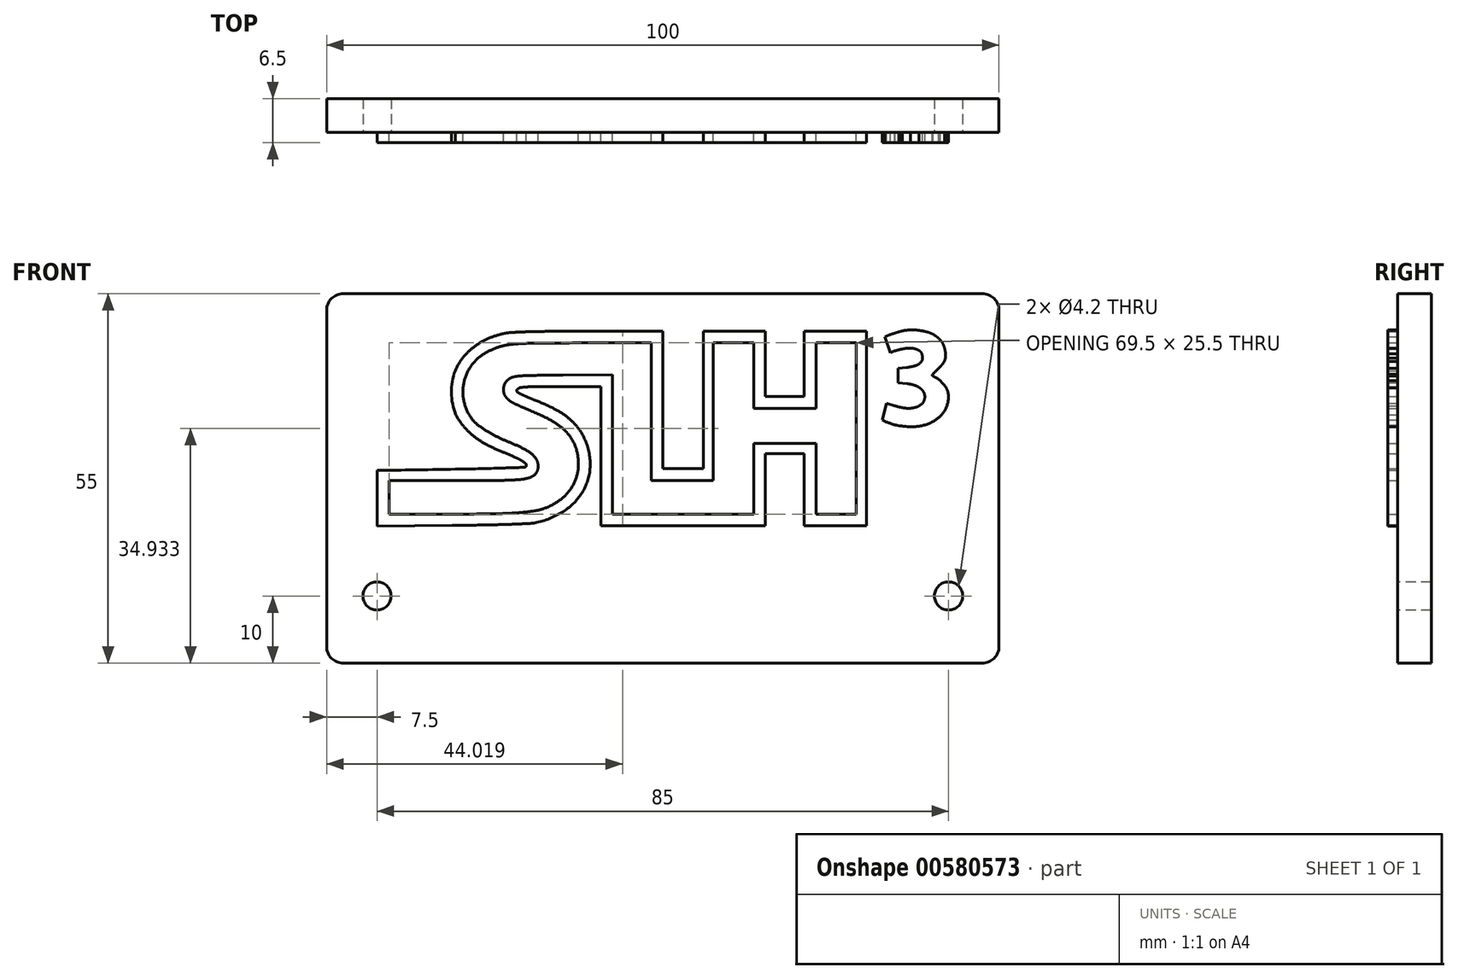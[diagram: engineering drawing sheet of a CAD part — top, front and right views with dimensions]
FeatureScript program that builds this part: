
annotation { "Feature Type Name" : "Feature", "Feature Type Description" : "" }
export const myFeature = defineFeature(function(context is Context, id is Id, definition is map)
    precondition{}
    {
        {
            var Q0;
            Q0=qCreatedBy(makeId("Front.planeOp"),FACE);
            var sketch = newSketch(context, id + "F0", { "sketchPlane" : qUnion([Q0])});
            skArc(sketch, "E0", {"start": v(147.3, 58.44) * mm, "mid": v(144.9, 58.22) * mm, "end": v(142.5, 57.82) * mm});
            skArc(sketch, "E1", {"start": v(142.5, 57.82) * mm, "mid": v(141.63, 57.59) * mm, "end": v(140.75, 57.35) * mm});
            skArc(sketch, "E2", {"start": v(140.75, 57.35) * mm, "mid": v(139.8, 57.05) * mm, "end": v(138.84, 56.75) * mm});
            skArc(sketch, "E3", {"start": v(138.84, 56.75) * mm, "mid": v(137.83, 56.42) * mm, "end": v(136.83, 56.09) * mm});
            skArc(sketch, "E4", {"start": v(136.83, 56.09) * mm, "mid": v(134.45, 55.26) * mm, "end": v(132.1, 54.33) * mm});
            skArc(sketch, "E5", {"start": v(135.3, 44.79) * mm, "mid": v(138.92, 46.14) * mm, "end": v(142.68, 47.08) * mm});
            skArc(sketch, "E6", {"start": v(142.68, 47.08) * mm, "mid": v(145.3, 47.46) * mm, "end": v(147.96, 47.48) * mm});
            skArc(sketch, "E7", {"start": v(147.96, 47.48) * mm, "mid": v(150, 47.16) * mm, "end": v(151.95, 46.48) * mm});
            skArc(sketch, "E8", {"start": v(151.95, 46.48) * mm, "mid": v(153.25, 45.54) * mm, "end": v(154.1, 44.19) * mm});
            skArc(sketch, "E9", {"start": v(154.1, 44.19) * mm, "mid": v(154.46, 42.68) * mm, "end": v(154.45, 41.13) * mm});
            skArc(sketch, "E10", {"start": v(154.45, 41.13) * mm, "mid": v(154.03, 39.82) * mm, "end": v(153.18, 38.74) * mm});
            skArc(sketch, "E11", {"start": v(153.18, 38.74) * mm, "mid": v(151.73, 37.71) * mm, "end": v(150.09, 37.04) * mm});
            skArc(sketch, "E12", {"start": v(150.09, 37.04) * mm, "mid": v(147.56, 36.44) * mm, "end": v(145, 36.04) * mm});
            skLineSegment(sketch, "E13", {"start": v(145, 36.04) * mm, "end": v(140.08, 35.45) * mm});
            skLineSegment(sketch, "E14", {"start": v(140.08, 35.45) * mm, "end": v(140.08, 31.23) * mm});
            skLineSegment(sketch, "E15", {"start": v(140.08, 31.23) * mm, "end": v(140.08, 27.01) * mm});
            skLineSegment(sketch, "E16", {"start": v(140.08, 27.01) * mm, "end": v(145.31, 26.4) * mm});
            skArc(sketch, "E17", {"start": v(145.31, 26.4) * mm, "mid": v(147.5, 26.03) * mm, "end": v(149.65, 25.5) * mm});
            skArc(sketch, "E18", {"start": v(149.65, 25.5) * mm, "mid": v(151.33, 24.84) * mm, "end": v(152.88, 23.93) * mm});
            skArc(sketch, "E19", {"start": v(152.88, 23.93) * mm, "mid": v(154.03, 22.94) * mm, "end": v(154.95, 21.74) * mm});
            skArc(sketch, "E20", {"start": v(154.95, 21.74) * mm, "mid": v(155.57, 20.42) * mm, "end": v(155.88, 19) * mm});
            skArc(sketch, "E21", {"start": v(155.88, 19) * mm, "mid": v(155.68, 16.9) * mm, "end": v(154.7, 15.06) * mm});
            skArc(sketch, "E22", {"start": v(154.7, 15.06) * mm, "mid": v(152.96, 13.47) * mm, "end": v(150.85, 12.44) * mm});
            skArc(sketch, "E23", {"start": v(150.85, 12.44) * mm, "mid": v(147.9, 11.8) * mm, "end": v(144.88, 11.77) * mm});
            skArc(sketch, "E24", {"start": v(144.88, 11.77) * mm, "mid": v(141.4, 12.3) * mm, "end": v(138.02, 13.25) * mm});
            skArc(sketch, "E25", {"start": v(130.58, 4.7) * mm, "mid": v(134.35, 3.08) * mm, "end": v(138.27, 1.86) * mm});
            skArc(sketch, "E26", {"start": v(138.27, 1.86) * mm, "mid": v(144.65, 0.87) * mm, "end": v(151.1, 0.91) * mm});
            skArc(sketch, "E27", {"start": v(151.1, 0.91) * mm, "mid": v(156.72, 2.08) * mm, "end": v(161.92, 4.5) * mm});
            skArc(sketch, "E28", {"start": v(161.92, 4.5) * mm, "mid": v(165.7, 7.66) * mm, "end": v(168.44, 11.76) * mm});
            skArc(sketch, "E29", {"start": v(168.44, 11.76) * mm, "mid": v(169.8, 16.35) * mm, "end": v(169.66, 21.14) * mm});
            skArc(sketch, "E30", {"start": v(169.66, 21.14) * mm, "mid": v(169.24, 22.6) * mm, "end": v(168.57, 23.97) * mm});
            skArc(sketch, "E31", {"start": v(168.57, 23.97) * mm, "mid": v(166.9, 26.2) * mm, "end": v(165.02, 28.24) * mm});
            skArc(sketch, "E32", {"start": v(165.02, 28.24) * mm, "mid": v(162.97, 29.65) * mm, "end": v(160.8, 30.87) * mm});
            skArc(sketch, "E33", {"start": v(160.8, 30.87) * mm, "mid": v(160.38, 31.45) * mm, "end": v(160.66, 32.1) * mm});
            skArc(sketch, "E34", {"start": v(160.66, 32.1) * mm, "mid": v(162.36, 33.8) * mm, "end": v(164.08, 35.5) * mm});
            skArc(sketch, "E35", {"start": v(164.08, 35.5) * mm, "mid": v(165.17, 36.63) * mm, "end": v(166.22, 37.8) * mm});
            skArc(sketch, "E36", {"start": v(166.22, 37.8) * mm, "mid": v(166.84, 38.64) * mm, "end": v(167.35, 39.53) * mm});
            skArc(sketch, "E37", {"start": v(167.35, 39.53) * mm, "mid": v(167.8, 40.5) * mm, "end": v(168.09, 41.53) * mm});
            skArc(sketch, "E38", {"start": v(168.09, 41.53) * mm, "mid": v(168.2, 42.88) * mm, "end": v(168.2, 44.24) * mm});
            skArc(sketch, "E39", {"start": v(168.2, 44.24) * mm, "mid": v(168, 45.88) * mm, "end": v(167.63, 47.49) * mm});
            skArc(sketch, "E40", {"start": v(167.63, 47.49) * mm, "mid": v(167.09, 49.15) * mm, "end": v(166.3, 50.72) * mm});
            skArc(sketch, "E41", {"start": v(166.3, 50.72) * mm, "mid": v(165.28, 52.17) * mm, "end": v(164.05, 53.45) * mm});
            skArc(sketch, "E42", {"start": v(164.05, 53.45) * mm, "mid": v(162.51, 54.68) * mm, "end": v(160.85, 55.74) * mm});
            skArc(sketch, "E43", {"start": v(160.85, 55.74) * mm, "mid": v(159.13, 56.56) * mm, "end": v(157.3, 57.16) * mm});
            skArc(sketch, "E44", {"start": v(157.3, 57.16) * mm, "mid": v(154.84, 57.72) * mm, "end": v(152.34, 58.13) * mm});
            skArc(sketch, "E45", {"start": v(152.34, 58.13) * mm, "mid": v(149.83, 58.36) * mm, "end": v(147.3, 58.44) * mm});
            skArc(sketch, "E46", {"start": v(-94.8, 56.19) * mm, "mid": v(-99.37, 54.96) * mm, "end": v(-103.8, 53.28) * mm});
            skArc(sketch, "E47", {"start": v(-103.8, 53.28) * mm, "mid": v(-107.86, 51.23) * mm, "end": v(-111.67, 48.76) * mm});
            skArc(sketch, "E48", {"start": v(-111.67, 48.76) * mm, "mid": v(-115.04, 45.97) * mm, "end": v(-118.08, 42.81) * mm});
            skArc(sketch, "E49", {"start": v(-118.08, 42.81) * mm, "mid": v(-121.12, 38.65) * mm, "end": v(-123.5, 34.08) * mm});
            skArc(sketch, "E50", {"start": v(-123.1, 7.94) * mm, "mid": v(-120.99, 4.39) * mm, "end": v(-118.53, 1.07) * mm});
            skArc(sketch, "E51", {"start": v(-118.53, 1.07) * mm, "mid": v(-115.75, -1.97) * mm, "end": v(-112.67, -4.7) * mm});
            skArc(sketch, "E52", {"start": v(-112.67, -4.7) * mm, "mid": v(-109, -7.38) * mm, "end": v(-105.1, -9.7) * mm});
            skArc(sketch, "E53", {"start": v(-105.1, -9.7) * mm, "mid": v(-100.3, -12.1) * mm, "end": v(-95.37, -14.24) * mm});
            skArc(sketch, "E54", {"start": v(-95.37, -14.24) * mm, "mid": v(-91.84, -15.69) * mm, "end": v(-88.34, -17.2) * mm});
            skArc(sketch, "E55", {"start": v(-88.34, -17.2) * mm, "mid": v(-86.15, -18.23) * mm, "end": v(-84.03, -19.4) * mm});
            skArc(sketch, "E56", {"start": v(-84.03, -19.4) * mm, "mid": v(-82.76, -20.23) * mm, "end": v(-81.57, -21.17) * mm});
            skArc(sketch, "E57", {"start": v(-81.57, -21.17) * mm, "mid": v(-81.17, -21.82) * mm, "end": v(-81.2, -22.58) * mm});
            skArc(sketch, "E58", {"start": v(-81.2, -22.58) * mm, "mid": v(-81.6, -23.16) * mm, "end": v(-82.27, -23.4) * mm});
            skArc(sketch, "E59", {"start": v(-82.27, -23.4) * mm, "mid": v(-89.42, -23.65) * mm, "end": v(-96.57, -23.9) * mm});
            skArc(sketch, "E60", {"start": v(-96.57, -23.9) * mm, "mid": v(-107.38, -24.2) * mm, "end": v(-118.18, -24.43) * mm});
            skArc(sketch, "E61", {"start": v(-118.18, -24.43) * mm, "mid": v(-139.68, -24.8) * mm, "end": v(-161.17, -25.13) * mm});
            skLineSegment(sketch, "E62", {"start": v(-161.17, -25.13) * mm, "end": v(-169.92, -25.27) * mm});
            skLineSegment(sketch, "E63", {"start": v(-169.92, -25.27) * mm, "end": v(-169.92, -41.9) * mm});
            skLineSegment(sketch, "E64", {"start": v(-169.92, -41.9) * mm, "end": v(-169.92, -58.54) * mm});
            skLineSegment(sketch, "E65", {"start": v(-169.92, -58.54) * mm, "end": v(-125.17, -58.01) * mm});
            skArc(sketch, "E66", {"start": v(-125.17, -58.01) * mm, "mid": v(-115.04, -57.88) * mm, "end": v(-104.91, -57.7) * mm});
            skArc(sketch, "E67", {"start": v(-104.91, -57.7) * mm, "mid": v(-97.51, -57.54) * mm, "end": v(-90.11, -57.31) * mm});
            skArc(sketch, "E68", {"start": v(-90.11, -57.31) * mm, "mid": v(-84.7, -57.1) * mm, "end": v(-79.27, -56.85) * mm});
            skArc(sketch, "E69", {"start": v(-79.27, -56.85) * mm, "mid": v(-77.08, -56.64) * mm, "end": v(-74.92, -56.25) * mm});
            skArc(sketch, "E70", {"start": v(-74.92, -56.25) * mm, "mid": v(-66.24, -53.43) * mm, "end": v(-58.23, -49.06) * mm});
            skArc(sketch, "E71", {"start": v(-58.23, -49.06) * mm, "mid": v(-51.9, -43.6) * mm, "end": v(-47.03, -36.8) * mm});
            skArc(sketch, "E72", {"start": v(-47.03, -36.8) * mm, "mid": v(-44.12, -29.35) * mm, "end": v(-43.18, -21.4) * mm});
            skArc(sketch, "E73", {"start": v(-43.18, -21.4) * mm, "mid": v(-44.2, -13.14) * mm, "end": v(-47.06, -5.32) * mm});
            skArc(sketch, "E74", {"start": v(-47.06, -5.32) * mm, "mid": v(-49.08, -1.82) * mm, "end": v(-51.5, 1.41) * mm});
            skArc(sketch, "E75", {"start": v(-51.5, 1.41) * mm, "mid": v(-54.35, 4.4) * mm, "end": v(-57.51, 7.02) * mm});
            skArc(sketch, "E76", {"start": v(-57.51, 7.02) * mm, "mid": v(-61.55, 9.74) * mm, "end": v(-65.82, 12.07) * mm});
            skArc(sketch, "E77", {"start": v(-65.82, 12.07) * mm, "mid": v(-71.57, 14.73) * mm, "end": v(-77.42, 17.15) * mm});
            skArc(sketch, "E78", {"start": v(-77.42, 17.15) * mm, "mid": v(-78.84, 17.71) * mm, "end": v(-80.25, 18.3) * mm});
            skArc(sketch, "E79", {"start": v(-80.25, 18.3) * mm, "mid": v(-81.6, 18.89) * mm, "end": v(-82.95, 19.5) * mm});
            skArc(sketch, "E80", {"start": v(-82.95, 19.5) * mm, "mid": v(-84.1, 20.05) * mm, "end": v(-85.23, 20.6) * mm});
            skArc(sketch, "E81", {"start": v(-85.23, 20.6) * mm, "mid": v(-85.84, 20.95) * mm, "end": v(-86.42, 21.34) * mm});
            skArc(sketch, "E82", {"start": v(-86.42, 21.34) * mm, "mid": v(-86.85, 22.1) * mm, "end": v(-86.6, 22.92) * mm});
            skArc(sketch, "E83", {"start": v(-86.6, 22.92) * mm, "mid": v(-85.66, 23.7) * mm, "end": v(-84.5, 24.07) * mm});
            skArc(sketch, "E84", {"start": v(-84.5, 24.07) * mm, "mid": v(-80.93, 24.44) * mm, "end": v(-77.35, 24.6) * mm});
            skArc(sketch, "E85", {"start": v(-77.35, 24.6) * mm, "mid": v(-69.26, 24.68) * mm, "end": v(-61.17, 24.72) * mm});
            skLineSegment(sketch, "E86", {"start": v(-61.17, 24.72) * mm, "end": v(-36.92, 24.73) * mm});
            skLineSegment(sketch, "E87", {"start": v(-36.92, 24.73) * mm, "end": v(-36.92, -16.77) * mm});
            skLineSegment(sketch, "E88", {"start": v(-36.92, -16.77) * mm, "end": v(-36.92, -58.27) * mm});
            skLineSegment(sketch, "E89", {"start": v(-36.92, -58.27) * mm, "end": v(12.08, -58.27) * mm});
            skLineSegment(sketch, "E90", {"start": v(12.08, -58.27) * mm, "end": v(61.08, -58.27) * mm});
            skLineSegment(sketch, "E91", {"start": v(61.08, -58.27) * mm, "end": v(61.08, -36.77) * mm});
            skLineSegment(sketch, "E92", {"start": v(61.08, -36.77) * mm, "end": v(61.08, -15.27) * mm});
            skLineSegment(sketch, "E93", {"start": v(61.08, -15.27) * mm, "end": v(72.58, -15.27) * mm});
            skLineSegment(sketch, "E94", {"start": v(72.58, -15.27) * mm, "end": v(84.08, -15.27) * mm});
            skLineSegment(sketch, "E95", {"start": v(84.08, -15.27) * mm, "end": v(84.08, -36.77) * mm});
            skLineSegment(sketch, "E96", {"start": v(84.08, -36.77) * mm, "end": v(84.08, -58.27) * mm});
            skLineSegment(sketch, "E97", {"start": v(84.08, -58.27) * mm, "end": v(102.58, -58.27) * mm});
            skLineSegment(sketch, "E98", {"start": v(102.58, -58.27) * mm, "end": v(121.08, -58.27) * mm});
            skLineSegment(sketch, "E99", {"start": v(121.08, -58.27) * mm, "end": v(121.08, -0.27) * mm});
            skLineSegment(sketch, "E100", {"start": v(121.08, -0.27) * mm, "end": v(121.08, 57.73) * mm});
            skLineSegment(sketch, "E101", {"start": v(121.08, 57.73) * mm, "end": v(102.58, 57.73) * mm});
            skLineSegment(sketch, "E102", {"start": v(102.58, 57.73) * mm, "end": v(84.08, 57.73) * mm});
            skLineSegment(sketch, "E103", {"start": v(84.08, 57.73) * mm, "end": v(84.08, 38.23) * mm});
            skLineSegment(sketch, "E104", {"start": v(84.08, 38.23) * mm, "end": v(84.08, 18.73) * mm});
            skLineSegment(sketch, "E105", {"start": v(84.08, 18.73) * mm, "end": v(72.58, 18.73) * mm});
            skLineSegment(sketch, "E106", {"start": v(72.58, 18.73) * mm, "end": v(61.08, 18.73) * mm});
            skLineSegment(sketch, "E107", {"start": v(61.08, 18.73) * mm, "end": v(61.08, 38.23) * mm});
            skLineSegment(sketch, "E108", {"start": v(61.08, 38.23) * mm, "end": v(61.08, 57.73) * mm});
            skLineSegment(sketch, "E109", {"start": v(61.08, 57.73) * mm, "end": v(42.58, 57.73) * mm});
            skLineSegment(sketch, "E110", {"start": v(42.58, 57.73) * mm, "end": v(24.08, 57.73) * mm});
            skLineSegment(sketch, "E111", {"start": v(24.08, 57.73) * mm, "end": v(24.08, 16.73) * mm});
            skLineSegment(sketch, "E112", {"start": v(24.08, 16.73) * mm, "end": v(24.08, -24.27) * mm});
            skLineSegment(sketch, "E113", {"start": v(24.08, -24.27) * mm, "end": v(12.08, -24.27) * mm});
            skLineSegment(sketch, "E114", {"start": v(12.08, -24.27) * mm, "end": v(0.08, -24.27) * mm});
            skLineSegment(sketch, "E115", {"start": v(0.08, -24.27) * mm, "end": v(0.08, 16.73) * mm});
            skLineSegment(sketch, "E116", {"start": v(0.08, 16.73) * mm, "end": v(0.08, 57.73) * mm});
            skLineSegment(sketch, "E117", {"start": v(0.08, 57.73) * mm, "end": v(-44.17, 57.65) * mm});
            skArc(sketch, "E118", {"start": v(-44.17, 57.65) * mm, "mid": v(-55.24, 57.62) * mm, "end": v(-66.31, 57.55) * mm});
            skArc(sketch, "E119", {"start": v(-66.31, 57.55) * mm, "mid": v(-73.3, 57.46) * mm, "end": v(-80.3, 57.3) * mm});
            skArc(sketch, "E120", {"start": v(-80.3, 57.3) * mm, "mid": v(-85.01, 57.12) * mm, "end": v(-89.72, 56.88) * mm});
            skArc(sketch, "E121", {"start": v(-89.72, 56.88) * mm, "mid": v(-92.27, 56.63) * mm, "end": v(-94.8, 56.19) * mm});
            skLineSegment(sketch, "E122", {"start": v(-6.92, 9.73) * mm, "end": v(-6.92, -31.27) * mm});
            skLineSegment(sketch, "E123", {"start": v(-6.92, -31.27) * mm, "end": v(11.58, -31.27) * mm});
            skLineSegment(sketch, "E124", {"start": v(11.58, -31.27) * mm, "end": v(30.08, -31.27) * mm});
            skLineSegment(sketch, "E125", {"start": v(30.08, -31.27) * mm, "end": v(30.08, 9.73) * mm});
            skLineSegment(sketch, "E126", {"start": v(30.08, 9.73) * mm, "end": v(30.08, 50.73) * mm});
            skLineSegment(sketch, "E127", {"start": v(30.08, 50.73) * mm, "end": v(42.08, 50.73) * mm});
            skLineSegment(sketch, "E128", {"start": v(42.08, 50.73) * mm, "end": v(54.08, 50.73) * mm});
            skLineSegment(sketch, "E129", {"start": v(54.08, 50.73) * mm, "end": v(54.08, 31.23) * mm});
            skLineSegment(sketch, "E130", {"start": v(54.08, 31.23) * mm, "end": v(54.08, 11.73) * mm});
            skLineSegment(sketch, "E131", {"start": v(54.08, 11.73) * mm, "end": v(72.58, 11.73) * mm});
            skLineSegment(sketch, "E132", {"start": v(72.58, 11.73) * mm, "end": v(91.08, 11.73) * mm});
            skLineSegment(sketch, "E133", {"start": v(91.08, 11.73) * mm, "end": v(91.08, 31.23) * mm});
            skLineSegment(sketch, "E134", {"start": v(91.08, 31.23) * mm, "end": v(91.08, 50.73) * mm});
            skLineSegment(sketch, "E135", {"start": v(91.08, 50.73) * mm, "end": v(103.08, 50.73) * mm});
            skLineSegment(sketch, "E136", {"start": v(103.08, 50.73) * mm, "end": v(115.08, 50.73) * mm});
            skLineSegment(sketch, "E137", {"start": v(115.08, 50.73) * mm, "end": v(115.08, -0.27) * mm});
            skLineSegment(sketch, "E138", {"start": v(115.08, -0.27) * mm, "end": v(115.08, -51.27) * mm});
            skLineSegment(sketch, "E139", {"start": v(115.08, -51.27) * mm, "end": v(103.08, -51.27) * mm});
            skLineSegment(sketch, "E140", {"start": v(103.08, -51.27) * mm, "end": v(91.08, -51.27) * mm});
            skLineSegment(sketch, "E141", {"start": v(91.08, -51.27) * mm, "end": v(91.08, -30.27) * mm});
            skLineSegment(sketch, "E142", {"start": v(91.08, -30.27) * mm, "end": v(91.08, -9.27) * mm});
            skLineSegment(sketch, "E143", {"start": v(91.08, -9.27) * mm, "end": v(72.58, -9.27) * mm});
            skLineSegment(sketch, "E144", {"start": v(72.58, -9.27) * mm, "end": v(54.08, -9.27) * mm});
            skLineSegment(sketch, "E145", {"start": v(54.08, -9.27) * mm, "end": v(54.08, -30.27) * mm});
            skLineSegment(sketch, "E146", {"start": v(54.08, -30.27) * mm, "end": v(54.08, -51.27) * mm});
            skLineSegment(sketch, "E147", {"start": v(54.08, -51.27) * mm, "end": v(12.08, -51.27) * mm});
            skLineSegment(sketch, "E148", {"start": v(12.08, -51.27) * mm, "end": v(-29.92, -51.27) * mm});
            skLineSegment(sketch, "E149", {"start": v(-29.92, -51.27) * mm, "end": v(-29.92, -9.71) * mm});
            skLineSegment(sketch, "E150", {"start": v(-29.92, -9.71) * mm, "end": v(-29.92, 31.84) * mm});
            skLineSegment(sketch, "E151", {"start": v(-29.92, 31.84) * mm, "end": v(-59.35, 31.54) * mm});
            skArc(sketch, "E152", {"start": v(-59.35, 31.54) * mm, "mid": v(-68.59, 31.43) * mm, "end": v(-77.82, 31.3) * mm});
            skArc(sketch, "E153", {"start": v(-77.82, 31.3) * mm, "mid": v(-81.4, 31.2) * mm, "end": v(-85, 30.98) * mm});
            skArc(sketch, "E154", {"start": v(-85, 30.98) * mm, "mid": v(-87, 30.75) * mm, "end": v(-88.97, 30.36) * mm});
            skArc(sketch, "E155", {"start": v(-88.97, 30.36) * mm, "mid": v(-90.35, 29.88) * mm, "end": v(-91.6, 29.13) * mm});
            skArc(sketch, "E156", {"start": v(-91.6, 29.13) * mm, "mid": v(-92.29, 28.57) * mm, "end": v(-92.92, 27.95) * mm});
            skArc(sketch, "E157", {"start": v(-92.92, 27.95) * mm, "mid": v(-93.42, 27.34) * mm, "end": v(-93.84, 26.68) * mm});
            skArc(sketch, "E158", {"start": v(-93.84, 26.68) * mm, "mid": v(-94.18, 25.95) * mm, "end": v(-94.43, 25.2) * mm});
            skArc(sketch, "E159", {"start": v(-94.43, 25.2) * mm, "mid": v(-94.62, 24.3) * mm, "end": v(-94.73, 23.39) * mm});
            skArc(sketch, "E160", {"start": v(-94.73, 23.39) * mm, "mid": v(-94.69, 21.74) * mm, "end": v(-94.29, 20.15) * mm});
            skArc(sketch, "E161", {"start": v(-94.29, 20.15) * mm, "mid": v(-93.54, 18.68) * mm, "end": v(-92.5, 17.41) * mm});
            skArc(sketch, "E162", {"start": v(-92.5, 17.41) * mm, "mid": v(-90.83, 16.03) * mm, "end": v(-88.98, 14.9) * mm});
            skArc(sketch, "E163", {"start": v(-88.98, 14.9) * mm, "mid": v(-86.09, 13.48) * mm, "end": v(-83.13, 12.2) * mm});
            skArc(sketch, "E164", {"start": v(-83.13, 12.2) * mm, "mid": v(-76.1, 9.22) * mm, "end": v(-69.2, 5.99) * mm});
            skArc(sketch, "E165", {"start": v(-69.2, 5.99) * mm, "mid": v(-64.63, 3.45) * mm, "end": v(-60.37, 0.44) * mm});
            skArc(sketch, "E166", {"start": v(-60.37, 0.44) * mm, "mid": v(-57.36, -2.33) * mm, "end": v(-54.8, -5.53) * mm});
            skArc(sketch, "E167", {"start": v(-54.8, -5.53) * mm, "mid": v(-52.8, -9.04) * mm, "end": v(-51.36, -12.83) * mm});
            skArc(sketch, "E168", {"start": v(-51.36, -12.83) * mm, "mid": v(-50.33, -18.12) * mm, "end": v(-50.26, -23.51) * mm});
            skArc(sketch, "E169", {"start": v(-50.26, -23.51) * mm, "mid": v(-51.18, -28.63) * mm, "end": v(-53.1, -33.46) * mm});
            skArc(sketch, "E170", {"start": v(-53.1, -33.46) * mm, "mid": v(-56, -37.9) * mm, "end": v(-59.7, -41.69) * mm});
            skArc(sketch, "E171", {"start": v(-59.7, -41.69) * mm, "mid": v(-64.29, -44.96) * mm, "end": v(-69.35, -47.44) * mm});
            skArc(sketch, "E172", {"start": v(-69.35, -47.44) * mm, "mid": v(-72.87, -48.6) * mm, "end": v(-76.49, -49.38) * mm});
            skArc(sketch, "E173", {"start": v(-76.49, -49.38) * mm, "mid": v(-81.5, -50.05) * mm, "end": v(-86.52, -50.5) * mm});
            skArc(sketch, "E174", {"start": v(-86.52, -50.5) * mm, "mid": v(-93.97, -50.9) * mm, "end": v(-101.43, -51.1) * mm});
            skArc(sketch, "E175", {"start": v(-101.43, -51.1) * mm, "mid": v(-113.71, -51.23) * mm, "end": v(-126, -51.27) * mm});
            skLineSegment(sketch, "E176", {"start": v(-126, -51.27) * mm, "end": v(-162.92, -51.27) * mm});
            skLineSegment(sketch, "E177", {"start": v(-162.92, -51.27) * mm, "end": v(-162.92, -41.27) * mm});
            skLineSegment(sketch, "E178", {"start": v(-162.92, -41.27) * mm, "end": v(-162.92, -31.27) * mm});
            skLineSegment(sketch, "E179", {"start": v(-162.92, -31.27) * mm, "end": v(-122.9, -31.27) * mm});
            skArc(sketch, "E180", {"start": v(-122.9, -31.27) * mm, "mid": v(-108.61, -31.24) * mm, "end": v(-94.33, -31.15) * mm});
            skArc(sketch, "E181", {"start": v(-94.33, -31.15) * mm, "mid": v(-88.88, -30.96) * mm, "end": v(-83.45, -30.5) * mm});
            skArc(sketch, "E182", {"start": v(-83.45, -30.5) * mm, "mid": v(-80.59, -29.95) * mm, "end": v(-77.85, -28.95) * mm});
            skArc(sketch, "E183", {"start": v(-77.85, -28.95) * mm, "mid": v(-76.05, -27.7) * mm, "end": v(-74.8, -25.9) * mm});
            skArc(sketch, "E184", {"start": v(-74.8, -25.9) * mm, "mid": v(-74.16, -23.65) * mm, "end": v(-74.23, -21.31) * mm});
            skArc(sketch, "E185", {"start": v(-74.23, -21.31) * mm, "mid": v(-75, -19.02) * mm, "end": v(-76.36, -17.03) * mm});
            skArc(sketch, "E186", {"start": v(-76.36, -17.03) * mm, "mid": v(-78.8, -14.77) * mm, "end": v(-81.58, -12.95) * mm});
            skArc(sketch, "E187", {"start": v(-81.58, -12.95) * mm, "mid": v(-85.86, -10.8) * mm, "end": v(-90.26, -8.91) * mm});
            skArc(sketch, "E188", {"start": v(-90.26, -8.91) * mm, "mid": v(-94.22, -7.25) * mm, "end": v(-98.12, -5.45) * mm});
            skArc(sketch, "E189", {"start": v(-98.12, -5.45) * mm, "mid": v(-101.59, -3.65) * mm, "end": v(-104.96, -1.68) * mm});
            skArc(sketch, "E190", {"start": v(-104.96, -1.68) * mm, "mid": v(-107.71, 0.13) * mm, "end": v(-110.36, 2.1) * mm});
            skArc(sketch, "E191", {"start": v(-110.36, 2.1) * mm, "mid": v(-112.17, 3.75) * mm, "end": v(-113.73, 5.62) * mm});
            skArc(sketch, "E192", {"start": v(-113.73, 5.62) * mm, "mid": v(-116.54, 10.5) * mm, "end": v(-118.28, 15.85) * mm});
            skArc(sketch, "E193", {"start": v(-118.28, 15.85) * mm, "mid": v(-118.88, 21.44) * mm, "end": v(-118.3, 27.04) * mm});
            skArc(sketch, "E194", {"start": v(-118.3, 27.04) * mm, "mid": v(-116.6, 32.37) * mm, "end": v(-113.82, 37.23) * mm});
            skArc(sketch, "E195", {"start": v(-113.82, 37.23) * mm, "mid": v(-110.1, 41.37) * mm, "end": v(-105.6, 44.63) * mm});
            skArc(sketch, "E196", {"start": v(-105.6, 44.63) * mm, "mid": v(-101.86, 46.53) * mm, "end": v(-97.96, 48.06) * mm});
            skArc(sketch, "E197", {"start": v(-97.96, 48.06) * mm, "mid": v(-94.07, 49.13) * mm, "end": v(-90.08, 49.77) * mm});
            skArc(sketch, "E198", {"start": v(-90.08, 49.77) * mm, "mid": v(-83.94, 50.27) * mm, "end": v(-77.78, 50.48) * mm});
            skArc(sketch, "E199", {"start": v(-77.78, 50.48) * mm, "mid": v(-62.98, 50.6) * mm, "end": v(-48.17, 50.67) * mm});
            skLineSegment(sketch, "E200", {"start": v(-48.17, 50.67) * mm, "end": v(-6.92, 50.73) * mm});
            skLineSegment(sketch, "E201", {"start": v(-6.92, 50.73) * mm, "end": v(-6.92, 9.73) * mm});
            skLineSegment(sketch, "E202", {"start": v(138.02, 13.25) * mm, "end": v(133.12, 14.81) * mm});
            skArc(sketch, "E203", {"start": v(-123.5, 34.08) * mm, "mid": v(-125.77, 20.97) * mm, "end": v(-123.1, 7.94) * mm});
            skLineSegment(sketch, "E204", {"start": v(133.12, 14.81) * mm, "end": v(130.58, 4.7) * mm});
            skLineSegment(sketch, "E205", {"start": v(132.1, 54.33) * mm, "end": v(135.3, 44.79) * mm});
            skSolve(sketch);
        }
        {
            var Q0;
            Q0=qSketchRegion(id+"F0",true);
            extrude(context, id + "F1", {"entities" : qUnion([Q0]), "depth" : 6 * mm, "offsetDistance" : 25 * mm});
        }
        {
            var Q0;
            Q0=makeQuery(id+"F1.opExtrude","SWEPT_BODY",BODY,{"disambiguationData":[OSD([sQuery(id+"F0.wireOp",EDGE,"E0"),sQuery(id+"F0.wireOp",EDGE,"E1"),sQuery(id+"F0.wireOp",EDGE,"E2"),sQuery(id+"F0.wireOp",EDGE,"E3"),sQuery(id+"F0.wireOp",EDGE,"E4"),sQuery(id+"F0.wireOp",EDGE,"E5"),sQuery(id+"F0.wireOp",EDGE,"E6"),sQuery(id+"F0.wireOp",EDGE,"E7"),sQuery(id+"F0.wireOp",EDGE,"E8"),sQuery(id+"F0.wireOp",EDGE,"E9"),sQuery(id+"F0.wireOp",EDGE,"E10"),sQuery(id+"F0.wireOp",EDGE,"E11"),sQuery(id+"F0.wireOp",EDGE,"E12"),sQuery(id+"F0.wireOp",EDGE,"E13"),sQuery(id+"F0.wireOp",EDGE,"E14"),sQuery(id+"F0.wireOp",EDGE,"E15"),sQuery(id+"F0.wireOp",EDGE,"E16"),sQuery(id+"F0.wireOp",EDGE,"E17"),sQuery(id+"F0.wireOp",EDGE,"E18"),sQuery(id+"F0.wireOp",EDGE,"E19"),sQuery(id+"F0.wireOp",EDGE,"E20"),sQuery(id+"F0.wireOp",EDGE,"E21"),sQuery(id+"F0.wireOp",EDGE,"E22"),sQuery(id+"F0.wireOp",EDGE,"E23"),sQuery(id+"F0.wireOp",EDGE,"E24"),sQuery(id+"F0.wireOp",EDGE,"E25"),sQuery(id+"F0.wireOp",EDGE,"E26"),sQuery(id+"F0.wireOp",EDGE,"E27"),sQuery(id+"F0.wireOp",EDGE,"E28"),sQuery(id+"F0.wireOp",EDGE,"E29"),sQuery(id+"F0.wireOp",EDGE,"E30"),sQuery(id+"F0.wireOp",EDGE,"E31"),sQuery(id+"F0.wireOp",EDGE,"E32"),sQuery(id+"F0.wireOp",EDGE,"E33"),sQuery(id+"F0.wireOp",EDGE,"E34"),sQuery(id+"F0.wireOp",EDGE,"E35"),sQuery(id+"F0.wireOp",EDGE,"E36"),sQuery(id+"F0.wireOp",EDGE,"E37"),sQuery(id+"F0.wireOp",EDGE,"E38"),sQuery(id+"F0.wireOp",EDGE,"E39"),sQuery(id+"F0.wireOp",EDGE,"E40"),sQuery(id+"F0.wireOp",EDGE,"E41"),sQuery(id+"F0.wireOp",EDGE,"E42"),sQuery(id+"F0.wireOp",EDGE,"E43"),sQuery(id+"F0.wireOp",EDGE,"E44"),sQuery(id+"F0.wireOp",EDGE,"E45"),sQuery(id+"F0.wireOp",EDGE,"E202"),sQuery(id+"F0.wireOp",EDGE,"E204"),sQuery(id+"F0.wireOp",EDGE,"E205")])]});
            var Q1;
            Q1=makeQuery(id+"F1.opExtrude","SWEPT_BODY",BODY,{"disambiguationData":[OSD([sQuery(id+"F0.wireOp",EDGE,"E46"),sQuery(id+"F0.wireOp",EDGE,"E47"),sQuery(id+"F0.wireOp",EDGE,"E48"),sQuery(id+"F0.wireOp",EDGE,"E49"),sQuery(id+"F0.wireOp",EDGE,"E50"),sQuery(id+"F0.wireOp",EDGE,"E51"),sQuery(id+"F0.wireOp",EDGE,"E52"),sQuery(id+"F0.wireOp",EDGE,"E53"),sQuery(id+"F0.wireOp",EDGE,"E54"),sQuery(id+"F0.wireOp",EDGE,"E55"),sQuery(id+"F0.wireOp",EDGE,"E56"),sQuery(id+"F0.wireOp",EDGE,"E57"),sQuery(id+"F0.wireOp",EDGE,"E58"),sQuery(id+"F0.wireOp",EDGE,"E59"),sQuery(id+"F0.wireOp",EDGE,"E60"),sQuery(id+"F0.wireOp",EDGE,"E61"),sQuery(id+"F0.wireOp",EDGE,"E62"),sQuery(id+"F0.wireOp",EDGE,"E63"),sQuery(id+"F0.wireOp",EDGE,"E64"),sQuery(id+"F0.wireOp",EDGE,"E65"),sQuery(id+"F0.wireOp",EDGE,"E66"),sQuery(id+"F0.wireOp",EDGE,"E67"),sQuery(id+"F0.wireOp",EDGE,"E68"),sQuery(id+"F0.wireOp",EDGE,"E69"),sQuery(id+"F0.wireOp",EDGE,"E70"),sQuery(id+"F0.wireOp",EDGE,"E71"),sQuery(id+"F0.wireOp",EDGE,"E72"),sQuery(id+"F0.wireOp",EDGE,"E73"),sQuery(id+"F0.wireOp",EDGE,"E74"),sQuery(id+"F0.wireOp",EDGE,"E75"),sQuery(id+"F0.wireOp",EDGE,"E76"),sQuery(id+"F0.wireOp",EDGE,"E77"),sQuery(id+"F0.wireOp",EDGE,"E78"),sQuery(id+"F0.wireOp",EDGE,"E79"),sQuery(id+"F0.wireOp",EDGE,"E80"),sQuery(id+"F0.wireOp",EDGE,"E81"),sQuery(id+"F0.wireOp",EDGE,"E82"),sQuery(id+"F0.wireOp",EDGE,"E83"),sQuery(id+"F0.wireOp",EDGE,"E84"),sQuery(id+"F0.wireOp",EDGE,"E85"),sQuery(id+"F0.wireOp",EDGE,"E86"),sQuery(id+"F0.wireOp",EDGE,"E87"),sQuery(id+"F0.wireOp",EDGE,"E88"),sQuery(id+"F0.wireOp",EDGE,"E89"),sQuery(id+"F0.wireOp",EDGE,"E90"),sQuery(id+"F0.wireOp",EDGE,"E91"),sQuery(id+"F0.wireOp",EDGE,"E92"),sQuery(id+"F0.wireOp",EDGE,"E93"),sQuery(id+"F0.wireOp",EDGE,"E94"),sQuery(id+"F0.wireOp",EDGE,"E95"),sQuery(id+"F0.wireOp",EDGE,"E96"),sQuery(id+"F0.wireOp",EDGE,"E97"),sQuery(id+"F0.wireOp",EDGE,"E98"),sQuery(id+"F0.wireOp",EDGE,"E99"),sQuery(id+"F0.wireOp",EDGE,"E100"),sQuery(id+"F0.wireOp",EDGE,"E101"),sQuery(id+"F0.wireOp",EDGE,"E102"),sQuery(id+"F0.wireOp",EDGE,"E103"),sQuery(id+"F0.wireOp",EDGE,"E104"),sQuery(id+"F0.wireOp",EDGE,"E105"),sQuery(id+"F0.wireOp",EDGE,"E106"),sQuery(id+"F0.wireOp",EDGE,"E107"),sQuery(id+"F0.wireOp",EDGE,"E108"),sQuery(id+"F0.wireOp",EDGE,"E109"),sQuery(id+"F0.wireOp",EDGE,"E110"),sQuery(id+"F0.wireOp",EDGE,"E111"),sQuery(id+"F0.wireOp",EDGE,"E112"),sQuery(id+"F0.wireOp",EDGE,"E113"),sQuery(id+"F0.wireOp",EDGE,"E114"),sQuery(id+"F0.wireOp",EDGE,"E115"),sQuery(id+"F0.wireOp",EDGE,"E116"),sQuery(id+"F0.wireOp",EDGE,"E117"),sQuery(id+"F0.wireOp",EDGE,"E118"),sQuery(id+"F0.wireOp",EDGE,"E119"),sQuery(id+"F0.wireOp",EDGE,"E120"),sQuery(id+"F0.wireOp",EDGE,"E121"),sQuery(id+"F0.wireOp",EDGE,"E122"),sQuery(id+"F0.wireOp",EDGE,"E123"),sQuery(id+"F0.wireOp",EDGE,"E124"),sQuery(id+"F0.wireOp",EDGE,"E125"),sQuery(id+"F0.wireOp",EDGE,"E126"),sQuery(id+"F0.wireOp",EDGE,"E127"),sQuery(id+"F0.wireOp",EDGE,"E128"),sQuery(id+"F0.wireOp",EDGE,"E129"),sQuery(id+"F0.wireOp",EDGE,"E130"),sQuery(id+"F0.wireOp",EDGE,"E131"),sQuery(id+"F0.wireOp",EDGE,"E132"),sQuery(id+"F0.wireOp",EDGE,"E133"),sQuery(id+"F0.wireOp",EDGE,"E134"),sQuery(id+"F0.wireOp",EDGE,"E135"),sQuery(id+"F0.wireOp",EDGE,"E136"),sQuery(id+"F0.wireOp",EDGE,"E137"),sQuery(id+"F0.wireOp",EDGE,"E138"),sQuery(id+"F0.wireOp",EDGE,"E139"),sQuery(id+"F0.wireOp",EDGE,"E140"),sQuery(id+"F0.wireOp",EDGE,"E141"),sQuery(id+"F0.wireOp",EDGE,"E142"),sQuery(id+"F0.wireOp",EDGE,"E143"),sQuery(id+"F0.wireOp",EDGE,"E144"),sQuery(id+"F0.wireOp",EDGE,"E145"),sQuery(id+"F0.wireOp",EDGE,"E146"),sQuery(id+"F0.wireOp",EDGE,"E147"),sQuery(id+"F0.wireOp",EDGE,"E148"),sQuery(id+"F0.wireOp",EDGE,"E149"),sQuery(id+"F0.wireOp",EDGE,"E150"),sQuery(id+"F0.wireOp",EDGE,"E151"),sQuery(id+"F0.wireOp",EDGE,"E152"),sQuery(id+"F0.wireOp",EDGE,"E153"),sQuery(id+"F0.wireOp",EDGE,"E154"),sQuery(id+"F0.wireOp",EDGE,"E155"),sQuery(id+"F0.wireOp",EDGE,"E156"),sQuery(id+"F0.wireOp",EDGE,"E157"),sQuery(id+"F0.wireOp",EDGE,"E158"),sQuery(id+"F0.wireOp",EDGE,"E159"),sQuery(id+"F0.wireOp",EDGE,"E160"),sQuery(id+"F0.wireOp",EDGE,"E161"),sQuery(id+"F0.wireOp",EDGE,"E162"),sQuery(id+"F0.wireOp",EDGE,"E163"),sQuery(id+"F0.wireOp",EDGE,"E164"),sQuery(id+"F0.wireOp",EDGE,"E165"),sQuery(id+"F0.wireOp",EDGE,"E166"),sQuery(id+"F0.wireOp",EDGE,"E167"),sQuery(id+"F0.wireOp",EDGE,"E168"),sQuery(id+"F0.wireOp",EDGE,"E169"),sQuery(id+"F0.wireOp",EDGE,"E170"),sQuery(id+"F0.wireOp",EDGE,"E171"),sQuery(id+"F0.wireOp",EDGE,"E172"),sQuery(id+"F0.wireOp",EDGE,"E173"),sQuery(id+"F0.wireOp",EDGE,"E174"),sQuery(id+"F0.wireOp",EDGE,"E175"),sQuery(id+"F0.wireOp",EDGE,"E176"),sQuery(id+"F0.wireOp",EDGE,"E177"),sQuery(id+"F0.wireOp",EDGE,"E178"),sQuery(id+"F0.wireOp",EDGE,"E179"),sQuery(id+"F0.wireOp",EDGE,"E180"),sQuery(id+"F0.wireOp",EDGE,"E181"),sQuery(id+"F0.wireOp",EDGE,"E182"),sQuery(id+"F0.wireOp",EDGE,"E183"),sQuery(id+"F0.wireOp",EDGE,"E184"),sQuery(id+"F0.wireOp",EDGE,"E185"),sQuery(id+"F0.wireOp",EDGE,"E186"),sQuery(id+"F0.wireOp",EDGE,"E187"),sQuery(id+"F0.wireOp",EDGE,"E188"),sQuery(id+"F0.wireOp",EDGE,"E189"),sQuery(id+"F0.wireOp",EDGE,"E190"),sQuery(id+"F0.wireOp",EDGE,"E191"),sQuery(id+"F0.wireOp",EDGE,"E192"),sQuery(id+"F0.wireOp",EDGE,"E193"),sQuery(id+"F0.wireOp",EDGE,"E194"),sQuery(id+"F0.wireOp",EDGE,"E195"),sQuery(id+"F0.wireOp",EDGE,"E196"),sQuery(id+"F0.wireOp",EDGE,"E197"),sQuery(id+"F0.wireOp",EDGE,"E198"),sQuery(id+"F0.wireOp",EDGE,"E199"),sQuery(id+"F0.wireOp",EDGE,"E200"),sQuery(id+"F0.wireOp",EDGE,"E201"),sQuery(id+"F0.wireOp",EDGE,"E203")])]});
            var Q2;
            Q2=qCreatedBy(makeId("Origin.pointOp"),VERTEX);
            transform(context, id + "F2", {"entities" : qUnion([Q0, Q1]), "transformType" : TransformType.SCALE_UNIFORMLY, "scale" : 0.25, "scalePoint" : qUnion([Q2]), "makeCopy" : false});
        }
        {
            var Q0;
            Q0=qCreatedBy(makeId("Front.planeOp"),FACE);
            var sketch = newSketch(context, id + "F3", { "sketchPlane" : qUnion([Q0])});
            skLineSegment(sketch, "E206.bottom", {"start": v(-50, 20) * mm, "end": v(50, 20) * mm});
            skLineSegment(sketch, "E206.top", {"start": v(-50, -35) * mm, "end": v(50, -35) * mm});
            skLineSegment(sketch, "E206.left", {"start": v(-50, 20) * mm, "end": v(-50, -35) * mm});
            skLineSegment(sketch, "E206.right", {"start": v(50, 20) * mm, "end": v(50, -35) * mm});
            skCircle(sketch, "E207", {"center": v(-42.5, -25) * mm, "radius": 2.1 * mm});
            skCircle(sketch, "E208", {"center": v(42.5, -25) * mm, "radius": 2.1 * mm});
            skLineSegment(sketch, "E209", {"start": v(-42.5, -25) * mm, "end": v(42.5, -25) * mm, "construction": true});
            skSolve(sketch);
        }
        {
            var Q0;
            Q0=qSketchRegion(id+"F3",true);
            extrude(context, id + "F4", {"entities" : qUnion([Q0]), "oppositeDirection" : true, "depth" : 5 * mm, "offsetDistance" : 25 * mm});
        }
        {
            var Q0;
            Q0=makeQuery(id+"F4.opExtrude","SWEPT_EDGE",EDGE,{"disambiguationData":[OSD([sQuery(id+"F3.wireOp",EDGE,"E206.bottom"),sQuery(id+"F3.wireOp",EDGE,"E206.left")])]});
            var Q1;
            Q1=makeQuery(id+"F4.opExtrude","SWEPT_EDGE",EDGE,{"disambiguationData":[OSD([sQuery(id+"F3.wireOp",EDGE,"E206.top"),sQuery(id+"F3.wireOp",EDGE,"E206.left")])]});
            var Q2;
            Q2=makeQuery(id+"F4.opExtrude","SWEPT_EDGE",EDGE,{"disambiguationData":[OSD([sQuery(id+"F3.wireOp",EDGE,"E206.top"),sQuery(id+"F3.wireOp",EDGE,"E206.right")])]});
            var Q3;
            Q3=makeQuery(id+"F4.opExtrude","SWEPT_EDGE",EDGE,{"disambiguationData":[OSD([sQuery(id+"F3.wireOp",EDGE,"E206.bottom"),sQuery(id+"F3.wireOp",EDGE,"E206.right")])]});
            fillet(context, id + "F5", {"entities" : qUnion([Q0, Q1, Q2, Q3]), "radius" : 2.5 * mm, "tangentPropagation" : true, "allowEdgeOverflow" : false});
        }
    });
